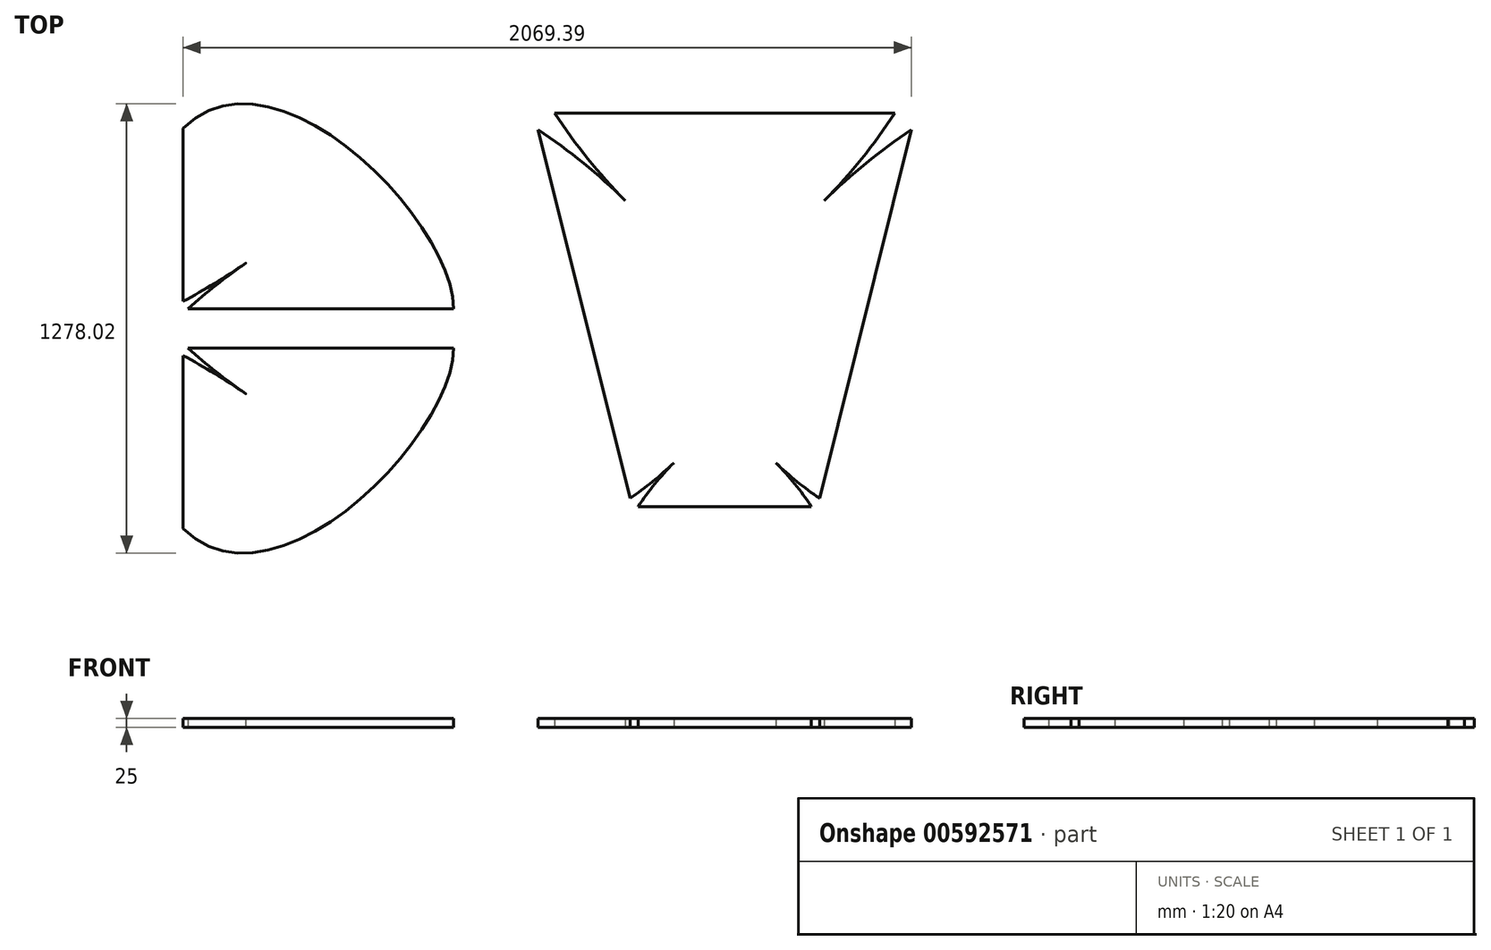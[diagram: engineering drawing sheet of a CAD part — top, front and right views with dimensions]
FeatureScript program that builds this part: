
annotation { "Feature Type Name" : "Feature", "Feature Type Description" : "" }
export const myFeature = defineFeature(function(context is Context, id is Id, definition is map)
    precondition{}
    {
        {
            var Q0;
            Q0=qCreatedBy(makeId("Top.planeOp"),FACE);
            var sketch = newSketch(context, id + "F0", { "sketchPlane" : qUnion([Q0])});
            skLineSegment(sketch, "E0.bottom", {"start": v(1200, 700) * mm, "end": v(-1200, 700) * mm});
            skLineSegment(sketch, "E0.top", {"start": v(1200, -700) * mm, "end": v(-1200, -700) * mm});
            skLineSegment(sketch, "E0.left", {"start": v(1200, 700) * mm, "end": v(1200, -700) * mm});
            skLineSegment(sketch, "E0.right", {"start": v(-1200, 700) * mm, "end": v(-1200, -700) * mm});
            skPoint(sketch, "E0.middle", {"position": v(0, 0) * mm});
            skSolve(sketch);
        }
        {
            var Q0;
            Q0=makeQuery(id+"F0.imprint","IMPRINT",FACE,{"disambiguationData":[TD([[makeQuery(id+"F0.imprint","IMPRINT",EDGE,{"derivedFrom":sQuery(id+"F0.wireOp",EDGE,"E0.bottom")}),1.0]])]});
            var sketch = newSketch(context, id + "F1", { "sketchPlane" : qUnion([Q0])});
            skLineSegment(sketch, "E1", {"start": v(-376.53, 318.03) * mm, "end": v(393.47, 318.03) * mm});
            skSolve(sketch);
        }
        {
            var Q0;
            Q0=qCreatedBy(makeId("Top.planeOp"),FACE);
            var sketch = newSketch(context, id + "F2", { "sketchPlane" : qUnion([Q0])});
            skLineSegment(sketch, "E2", {"start": v(344.59, -506.5) * mm, "end": v(362, -506.5) * mm, "construction": true});
            skLineSegment(sketch, "E3", {"start": v(1149.87, 611.88) * mm, "end": v(1138.22, 565.1) * mm, "construction": true});
            skLineSegment(sketch, "E4", {"start": v(66.03, 611.88) * mm, "end": v(125.01, 611.88) * mm, "construction": true});
            skLineSegment(sketch, "E5", {"start": v(607.95, 611.88) * mm, "end": v(607.95, -506.5) * mm, "construction": true});
            skPoint(sketch, "E6.orphan", {"position": v(1090.89, 611.88) * mm});
            skLineSegment(sketch, "E7.MirrorCS", {"start": v(66.03, 611.88) * mm, "end": v(77.68, 565.1) * mm, "construction": true});
            skPoint(sketch, "E8.orphan", {"position": v(125.01, 611.88) * mm});
            skPoint(sketch, "E9", {"position": v(325.53, 363.46) * mm});
            skPoint(sketch, "E10", {"position": v(463, -382) * mm});
            skPoint(sketch, "E11", {"position": v(362, -506.5) * mm});
            skPoint(sketch, "E12", {"position": v(338.7, -482.9) * mm});
            skPoint(sketch, "E13", {"position": v(77.68, 565.1) * mm});
            skArc(sketch, "E14", {"start": v(325.53, 363.46) * mm, "mid": v(206.43, 470.21) * mm, "end": v(77.68, 565.1) * mm});
            skArc(sketch, "E15", {"start": v(125.01, 611.88) * mm, "mid": v(218.94, 482.56) * mm, "end": v(325.53, 363.46) * mm});
            skArc(sketch, "E16", {"start": v(463, -382) * mm, "mid": v(409.32, -441.68) * mm, "end": v(362, -506.5) * mm});
            skArc(sketch, "E17", {"start": v(338.7, -482.9) * mm, "mid": v(403.06, -435.17) * mm, "end": v(463, -382) * mm});
            skArc(sketch, "E18.MirrorCS", {"start": v(1090.89, 611.88) * mm, "mid": v(996.96, 482.56) * mm, "end": v(890.37, 363.46) * mm});
            skArc(sketch, "E19.MirrorCS", {"start": v(890.37, 363.46) * mm, "mid": v(1009.47, 470.21) * mm, "end": v(1138.22, 565.1) * mm});
            skArc(sketch, "E20.MirrorCS", {"start": v(877.2, -482.9) * mm, "mid": v(812.84, -435.17) * mm, "end": v(752.9, -382) * mm});
            skArc(sketch, "E21.MirrorCS", {"start": v(752.9, -382) * mm, "mid": v(806.58, -441.68) * mm, "end": v(853.9, -506.5) * mm});
            skLineSegment(sketch, "E22", {"start": v(125.01, 611.88) * mm, "end": v(1090.89, 611.88) * mm});
            skLineSegment(sketch, "E23", {"start": v(77.68, 565.1) * mm, "end": v(338.7, -482.9) * mm});
            skLineSegment(sketch, "E24", {"start": v(338.7, -482.9) * mm, "end": v(344.59, -506.5) * mm, "construction": true});
            skLineSegment(sketch, "E25", {"start": v(362, -506.5) * mm, "end": v(853.9, -506.5) * mm});
            skLineSegment(sketch, "E26", {"start": v(853.9, -506.5) * mm, "end": v(871.32, -506.5) * mm, "construction": true});
            skLineSegment(sketch, "E27", {"start": v(877.2, -482.9) * mm, "end": v(871.32, -506.5) * mm, "construction": true});
            skLineSegment(sketch, "E28", {"start": v(1138.22, 565.1) * mm, "end": v(877.2, -482.9) * mm});
            skLineSegment(sketch, "E29", {"start": v(1090.89, 611.88) * mm, "end": v(1149.87, 611.88) * mm, "construction": true});
            skSolve(sketch);
        }
        {
            var Q0;
            Q0=qCreatedBy(makeId("Top.planeOp"),FACE);
            var sketch = newSketch(context, id + "F3", { "sketchPlane" : qUnion([Q0])});
            skPoint(sketch, "E30", {"position": v(-162.54, 56.39) * mm});
            skPoint(sketch, "E31", {"position": v(-931.17, 56.39) * mm});
            skPoint(sketch, "E32", {"position": v(-916.51, 56.39) * mm});
            skPoint(sketch, "E33", {"position": v(-746.7, 189.72) * mm});
            skPoint(sketch, "E34", {"position": v(-931.17, 568.94) * mm});
            skLineSegment(sketch, "E35", {"start": v(-162.54, 56.39) * mm, "end": v(-916.51, 56.39) * mm});
            skLineSegment(sketch, "E36", {"start": v(-931.17, 56.39) * mm, "end": v(-916.51, 56.39) * mm, "construction": true});
            skLineSegment(sketch, "E37", {"start": v(-931.17, 56.39) * mm, "end": v(-931.17, 76.93) * mm, "construction": true});
            skPoint(sketch, "E38", {"position": v(-931.17, 76.93) * mm});
            skArc(sketch, "E39", {"start": v(-752.85, 185.47) * mm, "mid": v(-836.64, 123.41) * mm, "end": v(-916.51, 56.39) * mm});
            skArc(sketch, "E40", {"start": v(-931.17, 76.93) * mm, "mid": v(-840.56, 128.82) * mm, "end": v(-752.86, 185.49) * mm});
            skFitSpline(sketch, "E41", {"points": [v(-931.17, 568.94) * mm, v(-162.54, 56.39) * mm], "startDerivative": vector(786.95, 777.59) * mm, "endDerivative": vector(-2.82, -739.13) * mm});
            skLineSegment(sketch, "E42", {"start": v(-931.17, 568.94) * mm, "end": v(-542.77, 568.94) * mm, "construction": true});
            skLineSegment(sketch, "E43", {"start": v(-760.15, 568.94) * mm, "end": v(-760.15, 639) * mm, "construction": true});
            skLineSegment(sketch, "E44", {"start": v(-322.66, 56.39) * mm, "end": v(-322.66, 379.81) * mm, "construction": true});
            skLineSegment(sketch, "E45", {"start": v(-322.66, 379.81) * mm, "end": v(-931.17, 379.81) * mm, "construction": true});
            skLineSegment(sketch, "E46", {"start": v(-542.77, 568.94) * mm, "end": v(-542.77, 56.39) * mm, "construction": true});
            skLineSegment(sketch, "E47", {"start": v(-931.17, 76.93) * mm, "end": v(-931.17, 568.94) * mm});
            skLineSegment(sketch, "E48", {"start": v(0, 0) * mm, "end": v(-1080.45, 0) * mm, "construction": true});
            skLineSegment(sketch, "E49.MirrorCS", {"start": v(-931.17, -56.39) * mm, "end": v(-916.51, -56.39) * mm, "construction": true});
            skLineSegment(sketch, "E50.MirrorCS", {"start": v(-931.17, -56.39) * mm, "end": v(-931.17, -76.93) * mm, "construction": true});
            skPoint(sketch, "E51.MirrorP", {"position": v(-931.17, -56.39) * mm});
            skPoint(sketch, "E52.MirrorP", {"position": v(-916.51, -56.39) * mm});
            skLineSegment(sketch, "E53.MirrorCS", {"start": v(-322.66, -379.81) * mm, "end": v(-931.17, -379.81) * mm, "construction": true});
            skLineSegment(sketch, "E54.MirrorCS", {"start": v(-931.17, -568.94) * mm, "end": v(-542.77, -568.94) * mm, "construction": true});
            skLineSegment(sketch, "E55.MirrorCS", {"start": v(-760.15, -568.94) * mm, "end": v(-760.15, -639) * mm, "construction": true});
            skPoint(sketch, "E56.MirrorP", {"position": v(-162.54, -56.39) * mm});
            skPoint(sketch, "E57.MirrorP", {"position": v(-746.7, -189.72) * mm});
            skFitSpline(sketch, "E58.MirrorCS", {"points": [v(-931.17, -568.94) * mm, v(-162.54, -56.39) * mm], "startDerivative": vector(786.95, -777.59) * mm, "endDerivative": vector(-2.82, 739.13) * mm});
            skArc(sketch, "E59.MirrorCS", {"start": v(-752.85, -185.47) * mm, "mid": v(-836.64, -123.41) * mm, "end": v(-916.51, -56.39) * mm});
            skPoint(sketch, "E60.MirrorP", {"position": v(-931.17, -76.93) * mm});
            skLineSegment(sketch, "E61.MirrorCS", {"start": v(-322.66, -56.39) * mm, "end": v(-322.66, -379.81) * mm, "construction": true});
            skLineSegment(sketch, "E62.MirrorCS", {"start": v(-162.54, -56.39) * mm, "end": v(-916.51, -56.39) * mm});
            skLineSegment(sketch, "E63.MirrorCS", {"start": v(-931.17, -76.93) * mm, "end": v(-931.17, -568.94) * mm});
            skLineSegment(sketch, "E64.MirrorCS", {"start": v(-542.77, -568.94) * mm, "end": v(-542.77, -56.39) * mm, "construction": true});
            skArc(sketch, "E65.MirrorCS", {"start": v(-931.17, -76.93) * mm, "mid": v(-840.56, -128.82) * mm, "end": v(-752.86, -185.49) * mm});
            skArc(sketch, "E66.filletArc", {"start": v(-752.85, 185.47) * mm, "mid": v(-752.85, 185.48) * mm, "end": v(-752.86, 185.49) * mm});
            skArc(sketch, "E67.filletArc", {"start": v(-752.86, -185.49) * mm, "mid": v(-752.85, -185.48) * mm, "end": v(-752.85, -185.47) * mm});
            skSolve(sketch);
        }
        {
            var Q0;
            Q0=makeQuery(id+"F2.imprint","IMPRINT",FACE,{"disambiguationData":[TD([[makeQuery(id+"F2.imprint","IMPRINT",EDGE,{"derivedFrom":sQuery(id+"F2.wireOp",EDGE,"E14")}),1.0]])]});
            var Q1;
            Q1=makeQuery(id+"F3.imprint","IMPRINT",FACE,{"disambiguationData":[TD([[makeQuery(id+"F3.imprint","IMPRINT",EDGE,{"derivedFrom":sQuery(id+"F3.wireOp",EDGE,"E35")}),-1.0]])]});
            var Q2;
            Q2=makeQuery(id+"F3.imprint","IMPRINT",FACE,{"disambiguationData":[TD([[makeQuery(id+"F3.imprint","IMPRINT",EDGE,{"derivedFrom":sQuery(id+"F3.wireOp",EDGE,"E58.MirrorCS")}),1.0]])]});
            extrude(context, id + "F4", {"entities" : qUnion([Q0, Q1, Q2]), "depth" : 25 * mm, "offsetDistance" : 25 * mm});
        }
    });
